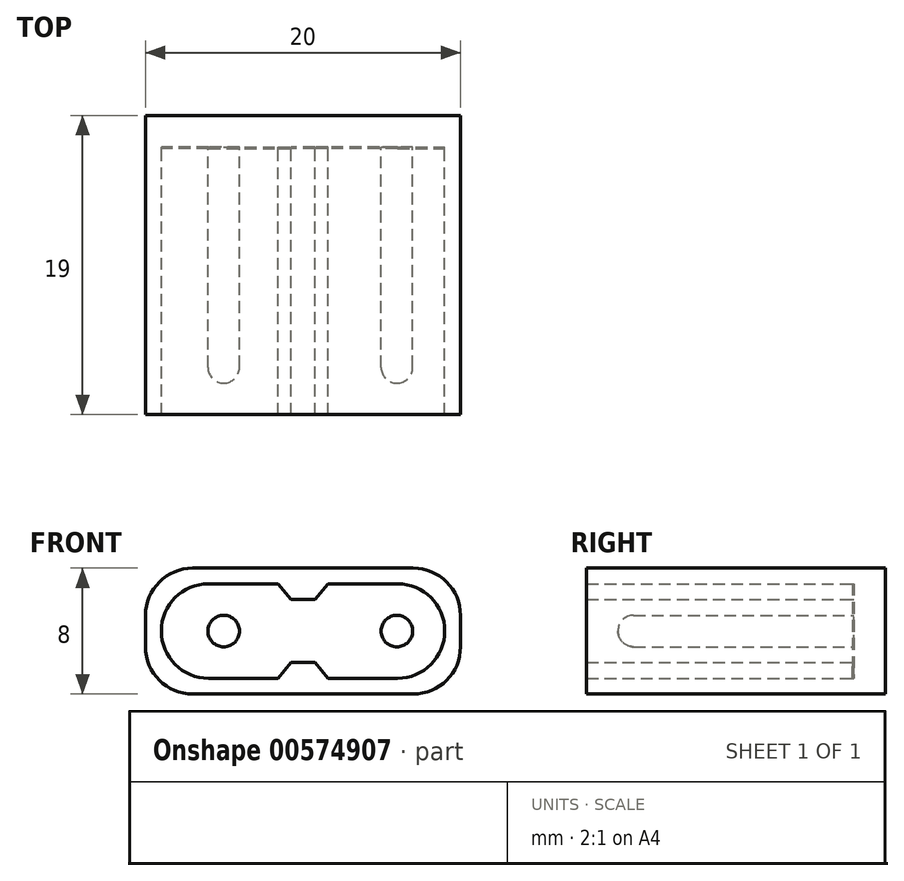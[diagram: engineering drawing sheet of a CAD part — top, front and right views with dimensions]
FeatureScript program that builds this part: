
annotation { "Feature Type Name" : "Feature", "Feature Type Description" : "" }
export const myFeature = defineFeature(function(context is Context, id is Id, definition is map)
    precondition{}
    {
        {
            var Q0;
            Q0=qCreatedBy(makeId("Front.planeOp"),FACE);
            var sketch = newSketch(context, id + "F0", { "sketchPlane" : qUnion([Q0])});
            skLineSegment(sketch, "E0.bottom", {"start": v(7, 4) * mm, "end": v(-7, 4) * mm});
            skLineSegment(sketch, "E0.top", {"start": v(7, -4) * mm, "end": v(-7, -4) * mm});
            skLineSegment(sketch, "E0.left", {"start": v(10, 1) * mm, "end": v(10, -1) * mm});
            skLineSegment(sketch, "E0.right", {"start": v(-10, 1) * mm, "end": v(-10, -1) * mm});
            skPoint(sketch, "E1.visualSharp", {"position": v(-10, 4) * mm});
            skArc(sketch, "E1.filletArc", {"start": v(-7, 4) * mm, "mid": v(-9.12, 3.12) * mm, "end": v(-10, 1) * mm});
            skPoint(sketch, "E2.visualSharp", {"position": v(-10, -4) * mm});
            skArc(sketch, "E2.filletArc", {"start": v(-10, -1) * mm, "mid": v(-9.12, -3.12) * mm, "end": v(-7, -4) * mm});
            skPoint(sketch, "E3.visualSharp", {"position": v(10, -4) * mm});
            skArc(sketch, "E3.filletArc", {"start": v(7, -4) * mm, "mid": v(9.12, -3.12) * mm, "end": v(10, -1) * mm});
            skPoint(sketch, "E4.visualSharp", {"position": v(10, 4) * mm});
            skArc(sketch, "E4.filletArc", {"start": v(10, 1) * mm, "mid": v(9.12, 3.12) * mm, "end": v(7, 4) * mm});
            skLineSegment(sketch, "E5", {"start": v(-6, 3) * mm, "end": v(-1.59, 3) * mm});
            skLineSegment(sketch, "E6", {"start": v(-1.59, 3) * mm, "end": v(-0.75, 2) * mm});
            skLineSegment(sketch, "E7", {"start": v(-0.75, 2) * mm, "end": v(0, 2) * mm});
            skLineSegment(sketch, "E8", {"start": v(-9, 0) * mm, "end": v(-9, 0) * mm});
            skArc(sketch, "E9", {"start": v(-9, 0) * mm, "mid": v(-8.12, 2.12) * mm, "end": v(-6, 3) * mm});
            skLineSegment(sketch, "E10.MirrorCS", {"start": v(0.75, 2) * mm, "end": v(0, 2) * mm});
            skLineSegment(sketch, "E11.MirrorCS", {"start": v(1.59, 3) * mm, "end": v(0.75, 2) * mm});
            skLineSegment(sketch, "E12.MirrorCS", {"start": v(6, 3) * mm, "end": v(1.59, 3) * mm});
            skArc(sketch, "E13.MirrorCS", {"start": v(9, 0) * mm, "mid": v(8.12, 2.12) * mm, "end": v(6, 3) * mm});
            skLineSegment(sketch, "E14.MirrorCS", {"start": v(9, 0) * mm, "end": v(9, 0) * mm});
            skArc(sketch, "E15.MirrorCS", {"start": v(9, 0) * mm, "mid": v(8.12, -2.12) * mm, "end": v(6, -3) * mm});
            skLineSegment(sketch, "E16.MirrorCS", {"start": v(6, -3) * mm, "end": v(1.59, -3) * mm});
            skLineSegment(sketch, "E17.MirrorCS", {"start": v(1.59, -3) * mm, "end": v(0.75, -2) * mm});
            skLineSegment(sketch, "E18.MirrorCS", {"start": v(0.75, -2) * mm, "end": v(0, -2) * mm});
            skLineSegment(sketch, "E19.MirrorCS", {"start": v(-0.75, -2) * mm, "end": v(0, -2) * mm});
            skLineSegment(sketch, "E20.MirrorCS", {"start": v(-1.59, -3) * mm, "end": v(-0.75, -2) * mm});
            skLineSegment(sketch, "E21.MirrorCS", {"start": v(-6, -3) * mm, "end": v(-1.59, -3) * mm});
            skArc(sketch, "E22.MirrorCS", {"start": v(-9, 0) * mm, "mid": v(-8.12, -2.12) * mm, "end": v(-6, -3) * mm});
            skSolve(sketch);
        }
        {
            var Q0;
            Q0 = qSketchRegion(id + "F0", true);
            extrude(context, id + "F1", {"entities" : qUnion([Q0]), "depth" : 17 * mm, "offsetDistance" : 25 * mm});
        }
        {
            var Q0;
            Q0=qCreatedBy(makeId("Front.planeOp"),FACE);
            var sketch = newSketch(context, id + "F2", { "sketchPlane" : qUnion([Q0])});
            skCircle(sketch, "E23", {"center": v(-5.04, 0) * mm, "radius": 1 * mm});
            skCircle(sketch, "E24", {"center": v(5.96, 0) * mm, "radius": 1 * mm});
            skSolve(sketch);
        }
        {
            var Q0;
            Q0 = qSketchRegion(id + "F2", true);
            extrude(context, id + "F3", {"entities" : qUnion([Q0]), "depth" : 15 * mm, "offsetDistance" : 25 * mm});
        }
        {
            var Q0;
            Q0=makeQuery(id+"F3.opExtrude","CAP_EDGE",EDGE,{"disambiguationData":[OSD([sQuery(id+"F2.wireOp",EDGE,"E23")])],"isStart":false});
            var Q1;
            Q1=makeQuery(id+"F3.opExtrude","CAP_EDGE",EDGE,{"disambiguationData":[OSD([sQuery(id+"F2.wireOp",EDGE,"E24")])],"isStart":false});
            fillet(context, id + "F4", {"entities" : qUnion([Q0, Q1]), "radius" : 1 * mm, "tangentPropagation" : true, "allowEdgeOverflow" : false});
        }
        {
            var Q0;
            Q0=makeQuery(id+"F0.imprint","IMPRINT",FACE,{"disambiguationData":[TD([[makeQuery(id+"F0.imprint","IMPRINT",EDGE,{"derivedFrom":sQuery(id+"F0.wireOp",EDGE,"E0.bottom")}),1.0]])]});
            var sketch = newSketch(context, id + "F5", { "sketchPlane" : qUnion([Q0])});
            skLineSegment(sketch, "E25.0", {"start": v(7, 4) * mm, "end": v(-7, 4) * mm});
            skPoint(sketch, "E26.0", {"position": v(9.12, 3.12) * mm});
            skArc(sketch, "E27.0", {"start": v(10, 1) * mm, "mid": v(9.12, 3.12) * mm, "end": v(7, 4) * mm});
            skLineSegment(sketch, "E28.0", {"start": v(10, 1) * mm, "end": v(10, -1) * mm});
            skArc(sketch, "E29.0", {"start": v(7, -4) * mm, "mid": v(9.12, -3.12) * mm, "end": v(10, -1) * mm});
            skLineSegment(sketch, "E30.0", {"start": v(7, -4) * mm, "end": v(-7, -4) * mm});
            skArc(sketch, "E31.0", {"start": v(-10, -1) * mm, "mid": v(-9.12, -3.12) * mm, "end": v(-7, -4) * mm});
            skLineSegment(sketch, "E32.0", {"start": v(-10, 1) * mm, "end": v(-10, -1) * mm});
            skArc(sketch, "E33.0", {"start": v(-7, 4) * mm, "mid": v(-9.12, 3.12) * mm, "end": v(-10, 1) * mm});
            skSolve(sketch);
        }
        {
            var Q0;
            Q0 = qSketchRegion(id + "F5", true);
            extrude(context, id + "F6", {"entities" : qUnion([Q0]), "operationType" : NewBodyOperationType.ADD, "oppositeDirection" : true, "depth" : 2 * mm, "offsetDistance" : 25 * mm});
        }
        {
            var Q0;
            Q0=makeQuery(id+"F6.opExtrude","CAP_FACE",FACE,{"disambiguationData":[OSD([sQuery(id+"F5.wireOp",EDGE,"E25.0"),sQuery(id+"F5.wireOp",EDGE,"E27.0"),sQuery(id+"F5.wireOp",EDGE,"E28.0"),sQuery(id+"F5.wireOp",EDGE,"E29.0"),sQuery(id+"F5.wireOp",EDGE,"E30.0"),sQuery(id+"F5.wireOp",EDGE,"E31.0"),sQuery(id+"F5.wireOp",EDGE,"E32.0"),sQuery(id+"F5.wireOp",EDGE,"E33.0")])],"isStart":true});
            var sketch = newSketch(context, id + "F7", { "sketchPlane" : qUnion([Q0])});
            skLineSegment(sketch, "E34.0.0", {"start": v(-1.59, 3) * mm, "end": v(-6, 3) * mm});
            skArc(sketch, "E34.0.1", {"start": v(-6, 3) * mm, "mid": v(-9, 0) * mm, "end": v(-6, -3) * mm});
            skLineSegment(sketch, "E34.0.2", {"start": v(-6, -3) * mm, "end": v(-1.59, -3) * mm});
            skLineSegment(sketch, "E34.0.3", {"start": v(-1.59, -3) * mm, "end": v(-0.75, -2) * mm});
            skLineSegment(sketch, "E34.0.4", {"start": v(-0.75, -2) * mm, "end": v(0.75, -2) * mm});
            skLineSegment(sketch, "E34.0.5", {"start": v(0.75, -2) * mm, "end": v(1.59, -3) * mm});
            skLineSegment(sketch, "E34.0.6", {"start": v(1.59, -3) * mm, "end": v(6, -3) * mm});
            skArc(sketch, "E34.0.7", {"start": v(6, -3) * mm, "mid": v(9, 0) * mm, "end": v(6, 3) * mm});
            skLineSegment(sketch, "E34.0.8", {"start": v(6, 3) * mm, "end": v(1.59, 3) * mm});
            skLineSegment(sketch, "E34.0.9", {"start": v(1.59, 3) * mm, "end": v(0.75, 2) * mm});
            skLineSegment(sketch, "E34.0.10", {"start": v(0.75, 2) * mm, "end": v(-0.75, 2) * mm});
            skLineSegment(sketch, "E34.0.11", {"start": v(-0.75, 2) * mm, "end": v(-1.59, 3) * mm});
            skSolve(sketch);
        }
        {
            var Q0;
            Q0 = qSketchRegion(id + "F7", true);
            extrude(context, id + "F8", {"entities" : qUnion([Q0]), "depth" : 0.1 * mm, "offsetDistance" : 25 * mm});
        }
    });
